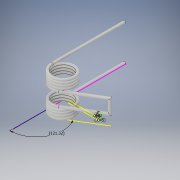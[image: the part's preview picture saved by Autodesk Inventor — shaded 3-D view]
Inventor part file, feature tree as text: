
AUTODESK INVENTOR PART (.ipt)
format: ipt  version: 2018 (Build 220112000, 112)  size: 438,272 bytes
history: native  units: in
note: dims shown in document units (in); Inventor stores cm internally (conversion verified against a paired STEP export)
features: sketch x18, extrude x15, projected_geometry x13, helix x1, plane x1, mirror x1
ambient origin geometry x8: Origin, YZ Plane, XZ Plane, XY Plane, X Axis, Y Axis, Z Axis, Center Point
bodies: Solid1 (feature_tree)
feature tree (49):
  helix  "Coil1"  [1 undecoded]
  extrude  "Extrusion1"  Depth=1.3in TaperAngle=0.0deg
  extrude  "Extrusion2"  Depth=0.0225in
  extrude  "Extrusion9"  Depth=0.35in TaperAngle=0.0deg
  extrude  "Extrusion11"  Depth=0.0225in
  sketch  "Sketch13"  dims[d44=0.0225in d45=1.0in d46=0.0in]
  extrude  "Extrusion12"  Depth=0.0225in TaperAngle=0.0deg
  extrude  "Extrusion13"  Depth=0.0984in
  extrude  "Extrusion14"  Depth=1.0in TaperAngle=0.0deg
  sketch  "Sketch19"  dims[d62=0.8336in d63=0.045in]
  sketch  "Sketch20"  dims[d64=2.0in d65=0.0in d66=2.0in d67=0.0in]
  plane  "Work Plane3"
  extrude  "Extrusion17"  Depth=0.045in
  mirror  "Mirror3"
  extrude  "Extrusion18"  Depth=0.045in
  sketch  "Sketch23"  dims[d72=2.0in d73=0.0in d74=2.0in d75=0.0in]
  extrude  "Extrusion20"  Depth=2.0in TaperAngle=0.0deg
  extrude  "Extrusion21"  Depth=2.0in TaperAngle=0.0deg
  extrude  "Extrusion22"  Depth=2.0in TaperAngle=0.0deg
  extrude  "Extrusion23"  [1 undecoded]
  extrude  "Extrusion24"  [1 undecoded]
  extrude  "Extrusion25"  [1 undecoded]
  sketch  "Sketch1"  dims[d1=0.215in]
  sketch  "Sketch2"  dims[d2=0.23in d3=0.2in d4=1.7075in d5=0.0in d6=90.0deg d7=90.0deg d8=0.0in d9=0.0in d10=1.3in d11=0.0in]
  projected_geometry  "Projected Loop1"
  sketch  "Sketch3"  dims[d12=0.7in d13=0.0in d32=0.0225in]
  sketch  "Sketch10"  dims[d33=0.35in d34=0.0in d37=0.35in d38=0.0in]
  projected_geometry  "Projected Loop5"
  sketch  "Sketch12"  dims[d41=1.0in d42=0.0in d43=0.0225in]
  projected_geometry  "Projected Loop7"
  projected_geometry  "Projected Loop8"
  sketch  "Sketch14"  dims[d47=1.0in d48=0.0in d53=0.0984in]
  projected_geometry  "Projected Loop9"
  sketch  "Sketch15"  dims[d54=0.1424in d55=1.0in d56=0.0in]
  sketch  "Sketch16"  dims[d57=1.0in d58=0.0in d61=0.045in]
  projected_geometry  "Projected Loop10"
  projected_geometry  "Projected Loop12"
  sketch  "Sketch21"  dims[d68=2.0in d69=0.0in d70=2.0in d71=0.0in]
  projected_geometry  "Projected Loop13"
  sketch  "Sketch24"
  projected_geometry  "Projected Loop15"
  sketch  "Sketch25"
  projected_geometry  "Projected Loop16"
  sketch  "Sketch26"
  projected_geometry  "Projected Loop17"
  sketch  "Sketch27"
  projected_geometry  "Projected Loop18"
  sketch  "Sketch28"
  projected_geometry  "Projected Loop19"
note: 4 required parameter values undecoded (feature->parameter linkage not recoverable at this tier; creation-order binding heuristic only, values carry confidence <= 0.55)
